# Revit family: Hager-GOLF-Flush_mounted-IP40-With_Cover-With_DIN-NoHosted-CH-it
name_source: partatom
category: Electrical Equipment
units: mm (PartAtom-declared; Revit-internal decimal feet)

## family parameters
Always vertical = Yes
Cut with Voids When Loaded = No
Maintain Annotation Orientation = No
Panel Configuration = Two Columns, Circuits Across
Part Type = Panelboard
Room Calculation Point = No
Round Connector Dimension = Use Diameter
Shared = No
Work Plane-Based = Yes

## types (20) — shared parameters
Code hager = ADD-EC000214_EU
Default Elevation = 1200 mm
EF000003 - modo di montaggio = incastrato
EF000007 - colore = bianco
EF000024 - resistente ai raggi UV = No
EF000049 - profondità = 97 mm  [stored 0.318241 ft]
EF000116 - numero RAL = 9010
EF000118 - con piastra di montaggio = No
EF000218 - profondità di montaggio = 72 mm  [stored 0.23622 ft]
EF001062 - versione EMC = No
EF001088 - possibilità di applicazione = Yes
EF001134 - barra DIN = Yes
EF004462 - tipo di chiusura = altri
EF005474 - grado di protezione (IP) = IP40
EF006306 - con serratura = No
EF009212 - tipo di coperchio = chiuso
EF015941 - porta di trasmissione del segnale = Yes
ETIM class code = EC000214
ETIM class name = Small distribution board
HG000001 - Numero di colonne = 1
HG000002-with door or cover-it = Yes
HG000003-Range-it = GOLF
HG000005-Thickness-it = 2 mm  [stored 0.00656168 ft]
HG000006-Flush mounted-it = Yes
HG000009-Double swing door-it = No
HG000010-Asymmetric doors-it = No
HG000011-Empty rows from bottom-it = No
HG000012-Door swing angle-it = 90.00°
HG000013-Door on the left-it = No
HG000014-Door on the right-it = Yes
HG000015-Clearance visibility-it = Yes
HG000016-Door 3D visibility-it = Yes
HG000017-Distance between poles-it = 18 mm  [stored 0.0590551 ft]
HG000060-RAL-number = 9010
HG000099-Onfly Template ID-it-CH = 507532
Manufacturer = Hager
Name = GOLF-Flush_mounted-IP40-With_Cover-With_DIN-CH
Name BIM&CO = Electricity
Name hager = ADD_Enclosures_EC000214
Uniformat = Low Tension Service & Dist.
Uniformat code = D501001
zero-valued in all types: EF001131 - profondità interna, HG000007-Number of empty columns-it, HG000008-Number of empty rows-it

## per-type parameters (varying)
| type | BC_METADATA | EF000008 - larghezza | EF000040 - altezza | EF000266 - numero di file | EF000332 - altezza di installazione | EF000846 - larghezza di montaggio | EF002950 - numero di unità modulari | EF006244 - coperchio/porta trasparente | EF015776 - morsetto di messa a terra | EF015777 - morsettiera a conduttore neutro | HG000004-Manufacturer reference-it | HGEF000266-Numero di file | HGEF0002950-larghezza in unità di suddivisione |
| GOLF-Flush_mounted_W204_H225_D97_4_Modular_Spacing-VF104PS | {"ObjectGuid":"d3b36538-3273-4197-a562-01bf94599a27","ModelGuid":"c720f5bf-d377-4fbb-8ea3-ddee08046793","VariantGuid":"7900b5fb-65a8-428c-881f-07103e9f7ffe","Revision":"#45","VariantName":"GOLF-Flush_mounted_W204_H225_D97_4_Modular_Spacing-VF104PS"} | 204 mm | 225 mm  [stored 0.738189 ft] | 1 | 189 mm  [stored 0.620079 ft] | 170 mm  [stored 0.557743 ft] | 4 | No | No | No | VF104PS | 1 | 4 |
| GOLF-Flush_mounted_W204_H225_D97_4_Modular_Spacing-VF104TS | {"ObjectGuid":"d3b36538-3273-4197-a562-01bf94599a27","ModelGuid":"c720f5bf-d377-4fbb-8ea3-ddee08046793","VariantGuid":"d0b361cd-5e5f-4586-98f2-c8f494179b52","Revision":"#45","VariantName":"GOLF-Flush_mounted_W204_H225_D97_4_Modular_Spacing-VF104TS"} | 204 mm | 225 mm  [stored 0.738189 ft] | 1 | 189 mm  [stored 0.620079 ft] | 170 mm  [stored 0.557743 ft] | 4 | Yes | No | No | VF104TS | 1 | 4 |
| GOLF-Flush_mounted_W275_H225_D97_8_Modular_Spacing-VF108PS | {"ObjectGuid":"d3b36538-3273-4197-a562-01bf94599a27","ModelGuid":"c720f5bf-d377-4fbb-8ea3-ddee08046793","VariantGuid":"570270ab-bc6c-4446-b563-185213bbcdad","Revision":"#45","VariantName":"GOLF-Flush_mounted_W275_H225_D97_8_Modular_Spacing-VF108PS"} | 275 mm | 225 mm  [stored 0.738189 ft] | 1 | 189 mm  [stored 0.620079 ft] | 242 mm  [stored 0.793963 ft] | 8 | No | No | No | VF108PS | 1 | 8 |
| GOLF-Flush_mounted_W275_H225_D97_8_Modular_Spacing-VF108TS | {"ObjectGuid":"d3b36538-3273-4197-a562-01bf94599a27","ModelGuid":"c720f5bf-d377-4fbb-8ea3-ddee08046793","VariantGuid":"a5ca7ae0-c990-4f4f-958b-64a5adfce291","Revision":"#45","VariantName":"GOLF-Flush_mounted_W275_H225_D97_8_Modular_Spacing-VF108TS"} | 275 mm | 225 mm  [stored 0.738189 ft] | 1 | 189 mm  [stored 0.620079 ft] | 242 mm  [stored 0.793963 ft] | 8 | Yes | No | No | VF108TS | 1 | 8 |
| GOLF-Flush_mounted_W352_H293_D97_12_Modular_Spacing-VF112PS | {"ObjectGuid":"d3b36538-3273-4197-a562-01bf94599a27","ModelGuid":"c720f5bf-d377-4fbb-8ea3-ddee08046793","VariantGuid":"727fad79-9f42-4d6a-8770-c75fea08dc77","Revision":"#45","VariantName":"GOLF-Flush_mounted_W352_H293_D97_12_Modular_Spacing-VF112PS"} | 352 mm  [stored 1.15486 ft] | 293 mm | 1 | 257 mm  [stored 0.843176 ft] | 318 mm  [stored 1.04331 ft] | 12 | No | Yes | Yes | VF112PS | 1 | 12 |
| GOLF-Flush_mounted_W352_H293_D97_12_Modular_Spacing-VF112TS | {"ObjectGuid":"d3b36538-3273-4197-a562-01bf94599a27","ModelGuid":"c720f5bf-d377-4fbb-8ea3-ddee08046793","VariantGuid":"401b5175-9fe8-49df-9ccf-2e24f019ef7c","Revision":"#45","VariantName":"GOLF-Flush_mounted_W352_H293_D97_12_Modular_Spacing-VF112TS"} | 352 mm  [stored 1.15486 ft] | 293 mm | 1 | 257 mm  [stored 0.843176 ft] | 318 mm  [stored 1.04331 ft] | 12 | Yes | Yes | Yes | VF112TS | 1 | 12 |
| GOLF-Flush_mounted_W460_H293_D97_18_Modular_Spacing-VF118PS | {"ObjectGuid":"d3b36538-3273-4197-a562-01bf94599a27","ModelGuid":"c720f5bf-d377-4fbb-8ea3-ddee08046793","VariantGuid":"17cf55a8-2466-4161-94ee-1b10718c4a4d","Revision":"#45","VariantName":"GOLF-Flush_mounted_W460_H293_D97_18_Modular_Spacing-VF118PS"} | 460 mm  [stored 1.50919 ft] | 293 mm | 1 | 257 mm  [stored 0.843176 ft] | 426 mm  [stored 1.39764 ft] | 18 | No | Yes | Yes | VF118PS | 1 | 18 |
| GOLF-Flush_mounted_W460_H293_D97_18_Modular_Spacing-VF118TS | {"ObjectGuid":"d3b36538-3273-4197-a562-01bf94599a27","ModelGuid":"c720f5bf-d377-4fbb-8ea3-ddee08046793","VariantGuid":"f1381982-cb5e-465f-aaa6-3617943f5a5b","Revision":"#45","VariantName":"GOLF-Flush_mounted_W460_H293_D97_18_Modular_Spacing-VF118TS"} | 460 mm  [stored 1.50919 ft] | 293 mm | 1 | 257 mm  [stored 0.843176 ft] | 426 mm  [stored 1.39764 ft] | 18 | Yes | Yes | Yes | VF118TS | 1 | 18 |
| GOLF-Flush_mounted_W532_H293_D97_22_Modular_Spacing-VF122PS | {"ObjectGuid":"d3b36538-3273-4197-a562-01bf94599a27","ModelGuid":"c720f5bf-d377-4fbb-8ea3-ddee08046793","VariantGuid":"c0cb78b3-62a0-4b84-8207-cc9b2857fa89","Revision":"#45","VariantName":"GOLF-Flush_mounted_W532_H293_D97_22_Modular_Spacing-VF122PS"} | 532 mm  [stored 1.74541 ft] | 293 mm | 1 | 257 mm  [stored 0.843176 ft] | 498 mm  [stored 1.63386 ft] | 22 | No | Yes | Yes | VF122PS | 1 | 22 |
| GOLF-Flush_mounted_W532_H293_D97_22_Modular_Spacing-VF122TS | {"ObjectGuid":"d3b36538-3273-4197-a562-01bf94599a27","ModelGuid":"c720f5bf-d377-4fbb-8ea3-ddee08046793","VariantGuid":"293e72b4-7d50-44bc-9811-b4883de919bd","Revision":"#45","VariantName":"GOLF-Flush_mounted_W532_H293_D97_22_Modular_Spacing-VF122TS"} | 532 mm  [stored 1.74541 ft] | 293 mm | 1 | 257 mm  [stored 0.843176 ft] | 498 mm  [stored 1.63386 ft] | 22 | Yes | Yes | Yes | VF122TS | 1 | 22 |
| GOLF-Flush_mounted_W382_H418_D97_12_Modular_Spacing-VF212PS | {"ObjectGuid":"d3b36538-3273-4197-a562-01bf94599a27","ModelGuid":"c720f5bf-d377-4fbb-8ea3-ddee08046793","VariantGuid":"1c1d9eb9-c584-4ae0-8d83-5a1a4a7ae2db","Revision":"#45","VariantName":"GOLF-Flush_mounted_W382_H418_D97_12_Modular_Spacing-VF212PS"} | 382 mm  [stored 1.25328 ft] | 418 mm  [stored 1.37139 ft] | 2 | 382 mm  [stored 1.25328 ft] | 318 mm  [stored 1.04331 ft] | 12 | No | Yes | Yes | VF212PS | 2 | 12 |
| GOLF-Flush_mounted_W382_H418_D97_12_Modular_Spacing-VF212TS | {"ObjectGuid":"d3b36538-3273-4197-a562-01bf94599a27","ModelGuid":"c720f5bf-d377-4fbb-8ea3-ddee08046793","VariantGuid":"b39c769c-76a6-433b-92f8-836be028bd5e","Revision":"#45","VariantName":"GOLF-Flush_mounted_W382_H418_D97_12_Modular_Spacing-VF212TS"} | 382 mm  [stored 1.25328 ft] | 418 mm  [stored 1.37139 ft] | 2 | 382 mm  [stored 1.25328 ft] | 318 mm  [stored 1.04331 ft] | 12 | Yes | Yes | Yes | VF212TS | 2 | 12 |
| GOLF-Flush_mounted_W460_H418_D97_18_Modular_Spacing-VF218PS | {"ObjectGuid":"d3b36538-3273-4197-a562-01bf94599a27","ModelGuid":"c720f5bf-d377-4fbb-8ea3-ddee08046793","VariantGuid":"c172c064-34f9-4b63-bcd4-669eb244d423","Revision":"#45","VariantName":"GOLF-Flush_mounted_W460_H418_D97_18_Modular_Spacing-VF218PS"} | 460 mm  [stored 1.50919 ft] | 418 mm  [stored 1.37139 ft] | 2 | 382 mm  [stored 1.25328 ft] | 426 mm  [stored 1.39764 ft] | 18 | No | Yes | Yes | VF218PS | 2 | 18 |
| GOLF-Flush_mounted_W460_H418_D97_18_Modular_Spacing-VF218TS | {"ObjectGuid":"d3b36538-3273-4197-a562-01bf94599a27","ModelGuid":"c720f5bf-d377-4fbb-8ea3-ddee08046793","VariantGuid":"49bc955d-51bb-46dd-88d1-44fea68c0c1f","Revision":"#45","VariantName":"GOLF-Flush_mounted_W460_H418_D97_18_Modular_Spacing-VF218TS"} | 460 mm  [stored 1.50919 ft] | 418 mm  [stored 1.37139 ft] | 2 | 382 mm  [stored 1.25328 ft] | 426 mm  [stored 1.39764 ft] | 18 | Yes | Yes | Yes | VF218TS | 2 | 18 |
| GOLF-Flush_mounted_W352_H543_D97_12_Modular_Spacing-VF312PS | {"ObjectGuid":"d3b36538-3273-4197-a562-01bf94599a27","ModelGuid":"c720f5bf-d377-4fbb-8ea3-ddee08046793","VariantGuid":"c3d42502-f03b-433e-aa45-f362adffbda1","Revision":"#45","VariantName":"GOLF-Flush_mounted_W352_H543_D97_12_Modular_Spacing-VF312PS"} | 352 mm  [stored 1.15486 ft] | 543 mm  [stored 1.7815 ft] | 3 | 507 mm  [stored 1.66339 ft] | 318 mm  [stored 1.04331 ft] | 12 | No | Yes | Yes | VF312PS | 3 | 12 |
| GOLF-Flush_mounted_W352_H543_D97_12_Modular_Spacing-VF312TS | {"ObjectGuid":"d3b36538-3273-4197-a562-01bf94599a27","ModelGuid":"c720f5bf-d377-4fbb-8ea3-ddee08046793","VariantGuid":"f244ddc7-7657-477c-902d-df50d8065ce0","Revision":"#45","VariantName":"GOLF-Flush_mounted_W352_H543_D97_12_Modular_Spacing-VF312TS"} | 352 mm  [stored 1.15486 ft] | 543 mm  [stored 1.7815 ft] | 3 | 507 mm  [stored 1.66339 ft] | 318 mm  [stored 1.04331 ft] | 12 | Yes | Yes | Yes | VF312TS | 3 | 12 |
| GOLF-Flush_mounted_W460_H543_D97_18_Modular_Spacing-VF318PS | {"ObjectGuid":"d3b36538-3273-4197-a562-01bf94599a27","ModelGuid":"c720f5bf-d377-4fbb-8ea3-ddee08046793","VariantGuid":"c54b9e4d-c32e-4291-85e6-d57d915798a3","Revision":"#45","VariantName":"GOLF-Flush_mounted_W460_H543_D97_18_Modular_Spacing-VF318PS"} | 460 mm  [stored 1.50919 ft] | 543 mm  [stored 1.7815 ft] | 3 | 507 mm  [stored 1.66339 ft] | 426 mm  [stored 1.39764 ft] | 18 | No | Yes | Yes | VF318PS | 3 | 18 |
| GOLF-Flush_mounted_W460_H543_D97_18_Modular_Spacing-VF318TS | {"ObjectGuid":"d3b36538-3273-4197-a562-01bf94599a27","ModelGuid":"c720f5bf-d377-4fbb-8ea3-ddee08046793","VariantGuid":"40748570-5609-4b70-acc0-c072c51e99ec","Revision":"#45","VariantName":"GOLF-Flush_mounted_W460_H543_D97_18_Modular_Spacing-VF318TS"} | 460 mm  [stored 1.50919 ft] | 543 mm  [stored 1.7815 ft] | 3 | 507 mm  [stored 1.66339 ft] | 426 mm  [stored 1.39764 ft] | 18 | Yes | Yes | Yes | VF318TS | 3 | 18 |
| GOLF-Flush_mounted_W352_H688_D97_12_Modular_Spacing-VF412PS | {"ObjectGuid":"d3b36538-3273-4197-a562-01bf94599a27","ModelGuid":"c720f5bf-d377-4fbb-8ea3-ddee08046793","VariantGuid":"b52c81ad-5181-4532-9eef-0566acd4b8b8","Revision":"#45","VariantName":"GOLF-Flush_mounted_W352_H688_D97_12_Modular_Spacing-VF412PS"} | 352 mm  [stored 1.15486 ft] | 688 mm  [stored 2.25722 ft] | 4 | 652 mm  [stored 2.13911 ft] | 318 mm  [stored 1.04331 ft] | 12 | No | Yes | Yes | VF412PS | 4 | 12 |
| GOLF-Flush_mounted_W460_H688_D97_18_Modular_Spacing-VF418PS | {"ObjectGuid":"d3b36538-3273-4197-a562-01bf94599a27","ModelGuid":"c720f5bf-d377-4fbb-8ea3-ddee08046793","VariantGuid":"9c3bfeb1-8f96-4eba-b4b7-d07036a65564","Revision":"#45","VariantName":"GOLF-Flush_mounted_W460_H688_D97_18_Modular_Spacing-VF418PS"} | 460 mm  [stored 1.50919 ft] | 688 mm  [stored 2.25722 ft] | 4 | 652 mm  [stored 2.13911 ft] | 426 mm  [stored 1.39764 ft] | 18 | No | Yes | Yes | VF418PS | 4 | 18 |

note: column(s) folded — value = type name in every type: Reference

note: [stored X ft] marks values corroborated as IEEE doubles in the binary element streams (Revit-internal decimal feet)

## geometry (parser evidence)
native form markers: Sweep x16
no freeform markers — native parametric forms only
